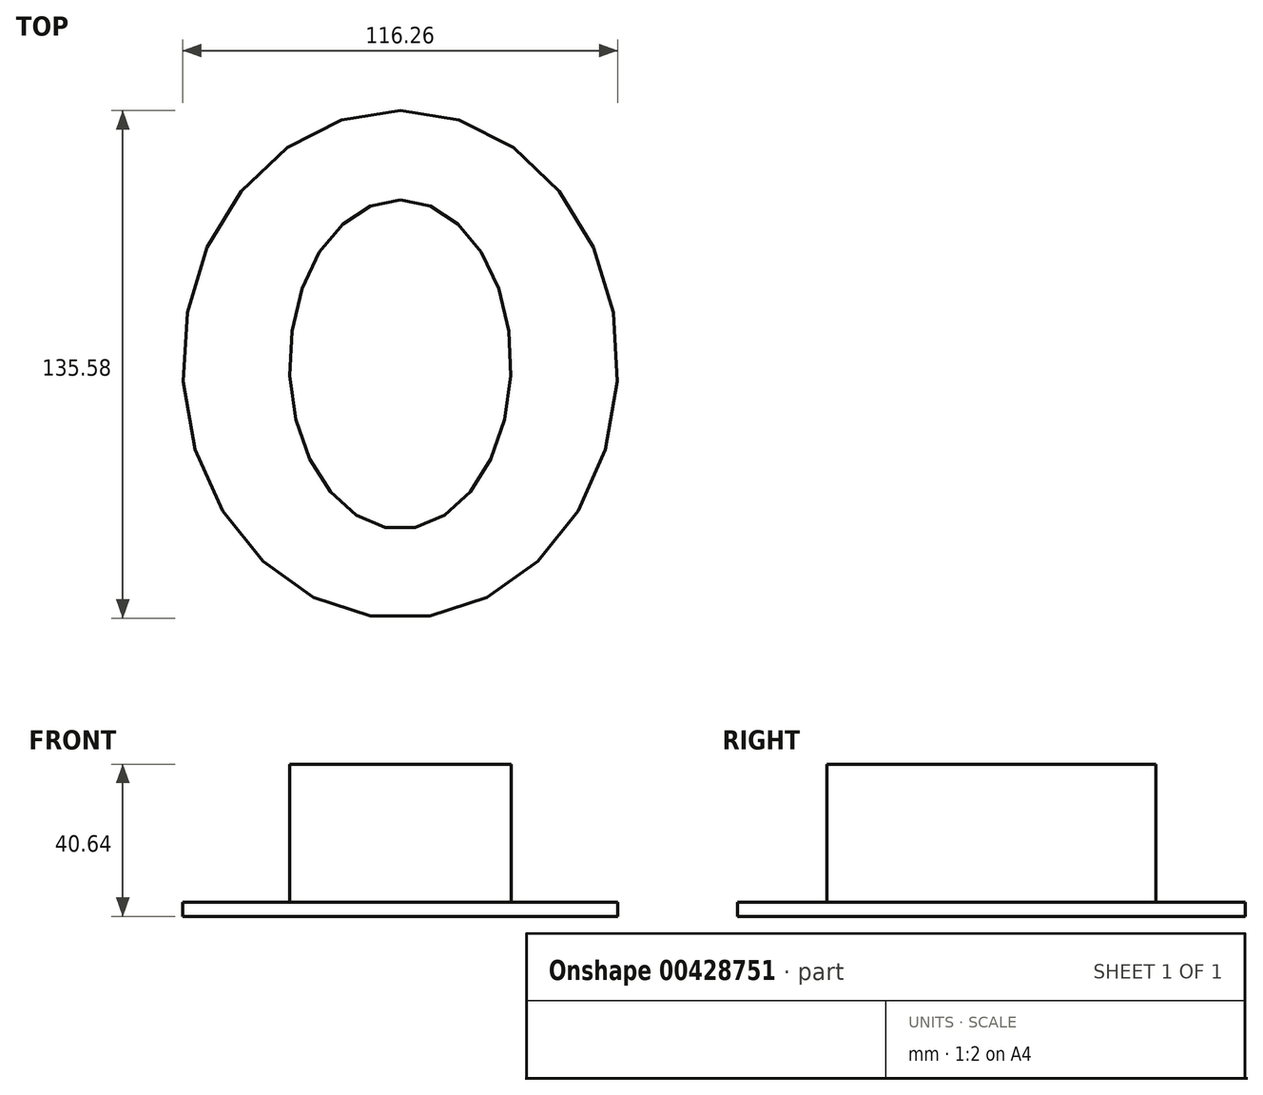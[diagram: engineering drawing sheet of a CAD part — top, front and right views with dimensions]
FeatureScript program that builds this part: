
annotation { "Feature Type Name" : "Feature", "Feature Type Description" : "" }
export const myFeature = defineFeature(function(context is Context, id is Id, definition is map)
    precondition{}
    {
        {
            var Q0;
            Q0=qCreatedBy(makeId("Top.planeOp"),FACE);
            var sketch = newSketch(context, id + "F0", { "sketchPlane" : qUnion([Q0])});
            skEllipse(sketch, "E0", {"center": v(0, 0) * mm, "majorRadius": 43.92 * mm, "minorRadius": 29.6 * mm, "majorAxis": v(0, 1)});
            skEllipse(sketch, "E1", {"center": v(0, 0) * mm, "majorRadius": 67.79 * mm, "minorRadius": 58.13 * mm, "majorAxis": v(0, 1)});
            skSolve(sketch);
        }
        {
            var Q0;
            Q0=makeQuery(id+"F0.imprint","IMPRINT",FACE,{"disambiguationData":[TD([[makeQuery(id+"F0.imprint","IMPRINT",EDGE,{"derivedFrom":sQuery(id+"F0.wireOp",EDGE,"E0")}),1.0]])]});
            extrude(context, id + "F1", {"entities" : qUnion([Q0]), "depth" : 40.64 * mm});
        }
        {
            var Q0;
            Q0 = qSketchRegion(id + "F0", true);
            extrude(context, id + "F2", {"entities" : qUnion([Q0]), "operationType" : NewBodyOperationType.ADD, "depth" : 3.8 * mm});
        }
    });
